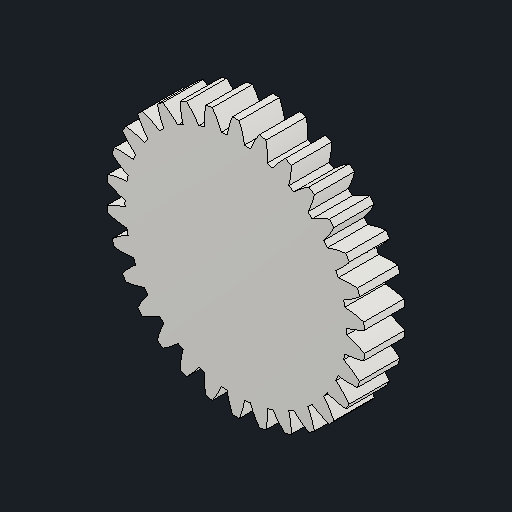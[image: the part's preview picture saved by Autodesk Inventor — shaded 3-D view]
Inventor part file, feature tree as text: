
AUTODESK INVENTOR PART (.ipt)
format: ipt  version: 2023.2 (Build 272271030, 271C)  size: 244,224 bytes
history: native  units: mm (DEFAULTED — no unit token found)
features: plane x3, other x3, sketch x2, extrude x1
ambient origin geometry x8: Origin, YZ Plane, XZ Plane, XY Plane, X Axis, Y Axis, Z Axis, Center Point
bodies: Solid1 (feature_tree)
feature tree (9):
  extrude  "Extrusion1"  Depth=5.0mm TaperAngle=0.0deg
  plane  "Work Plane2"
  plane  "Work Plane8"
  plane  "Work Plane9"
  other  "Spur Gear"
  sketch  "Sketch1"  dims[d0=32.0mm d1=5.0mm d2=0.0mm]
  sketch  "Sketch2"  dims[d3=30.0mm d4=10.0mm d5=0.0mm d16=19.0mm d17=0.0mm d34=1.047198mm d39=0.0mm d41=0.0mm d43=19.0mm d46=19.0mm d47=0.0mm d48=0.0mm]
  other  "Srf1"
  other  "Pitch Diameter"
